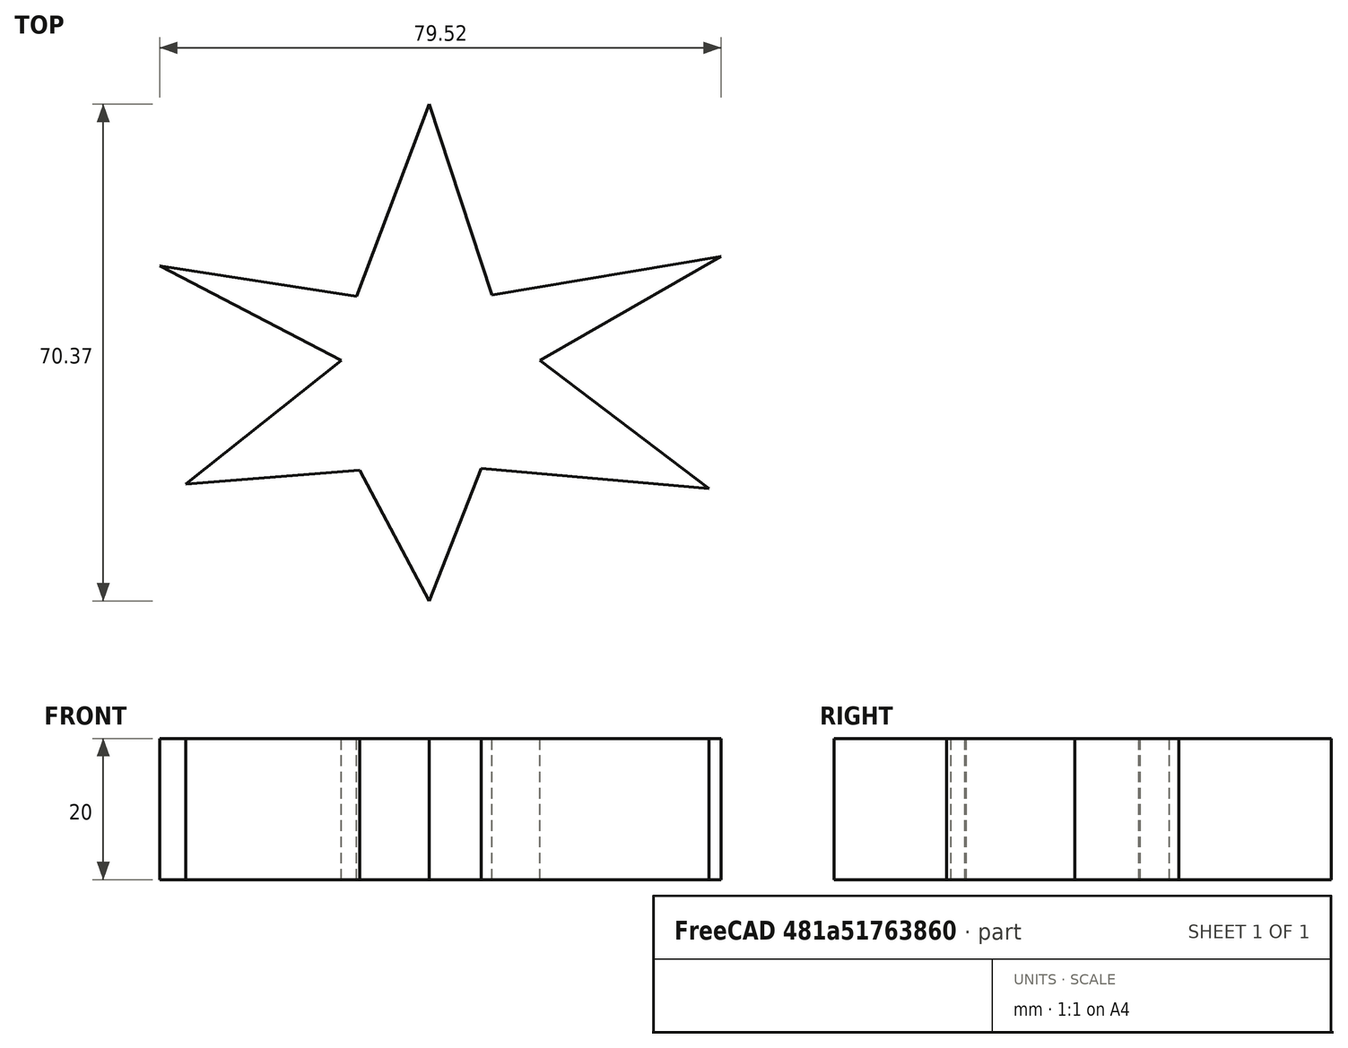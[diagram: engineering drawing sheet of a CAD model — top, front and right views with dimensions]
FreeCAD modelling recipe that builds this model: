
FCSTD DOCUMENT  (FreeCAD 0.21R33694 (Git))
Label: OJT1_T016_estrella
License: All rights reserved
LicenseURL: https://en.wikipedia.org/wiki/All_rights_reserved
objects: Sketcher::SketchObject×1, PartDesign::Pad×1, PartDesign::Body×1
note: 4 computed .brp shape members not serialized (recipe doc carries the construction recipe); baked Part::Feature solids carry a one-line shape summary decoded from their .brp

FEATURE [Sketcher::SketchObject] Sketch
  FullyConstrained = false
  MapMode = 5
  Support = -> [XY_Plane]
  sketch-geometry (12):
    g0: LineSegment StartX=0 StartY=36.2745 StartZ=0 EndX=8.93246 EndY=9.25926 EndZ=0
    g1: LineSegment StartX=8.93246 StartY=9.25926 StartZ=0 EndX=41.3943 EndY=14.7059 EndZ=0
    g2: LineSegment StartX=41.3943 StartY=14.7059 StartZ=0 EndX=15.6863 EndY=0 EndZ=0
    g3: LineSegment StartX=15.6863 StartY=0 StartZ=0 EndX=39.6514 EndY=-18.1917 EndZ=0
    g4: LineSegment StartX=39.6514 StartY=-18.1917 StartZ=0 EndX=7.40741 EndY=-15.3595 EndZ=0
    g5: LineSegment StartX=7.40741 StartY=-15.3595 StartZ=0 EndX=0 EndY=-34.0959 EndZ=0
    g6: LineSegment StartX=0 StartY=-34.0959 StartZ=0 EndX=-9.80392 EndY=-15.5773 EndZ=0
    g7: LineSegment StartX=-9.80392 StartY=-15.5773 StartZ=0 EndX=-34.4227 EndY=-17.5381 EndZ=0
    g8: LineSegment StartX=-34.4227 StartY=-17.5381 StartZ=0 EndX=-12.4183 EndY=0 EndZ=0
    g9: LineSegment StartX=-12.4183 StartY=0 StartZ=0 EndX=-38.1264 EndY=13.3987 EndZ=0
    g10: LineSegment StartX=-38.1264 StartY=13.3987 StartZ=0 EndX=-10.2396 EndY=9.04139 EndZ=0
    g11: LineSegment StartX=-10.2396 StartY=9.04139 StartZ=0 EndX=0 EndY=36.2745 EndZ=0
  constraints (16):
    c: PointOnObject(g0,g-2)
    c: Coincident(g1,g0)
    c: Coincident(g2,g1)
    c: PointOnObject(g2,g-1)
    c: Coincident(g3,g2)
    c: Coincident(g4,g3)
    c: Coincident(g5,g4)
    c: PointOnObject(g5,g-2)
    c: Coincident(g6,g5)
    c: Coincident(g7,g6)
    c: Coincident(g8,g7)
    c: PointOnObject(g8,g-1)
    c: Coincident(g9,g8)
    c: Coincident(g10,g9)
    c: Coincident(g11,g10)
    c: Coincident(g11,g0)
FEATURE [PartDesign::Pad] Pad
  Direction = (0,0,1)
  Length = 20
  Length2 = 10
  Profile = -> Sketch
  ReferenceAxis = -> Sketch [N_Axis]
  Type = 0
FEATURE [PartDesign::Body] Body
  Group = -> [Sketch,Pad]
  Origin = -> Origin
  Tip = -> Pad
